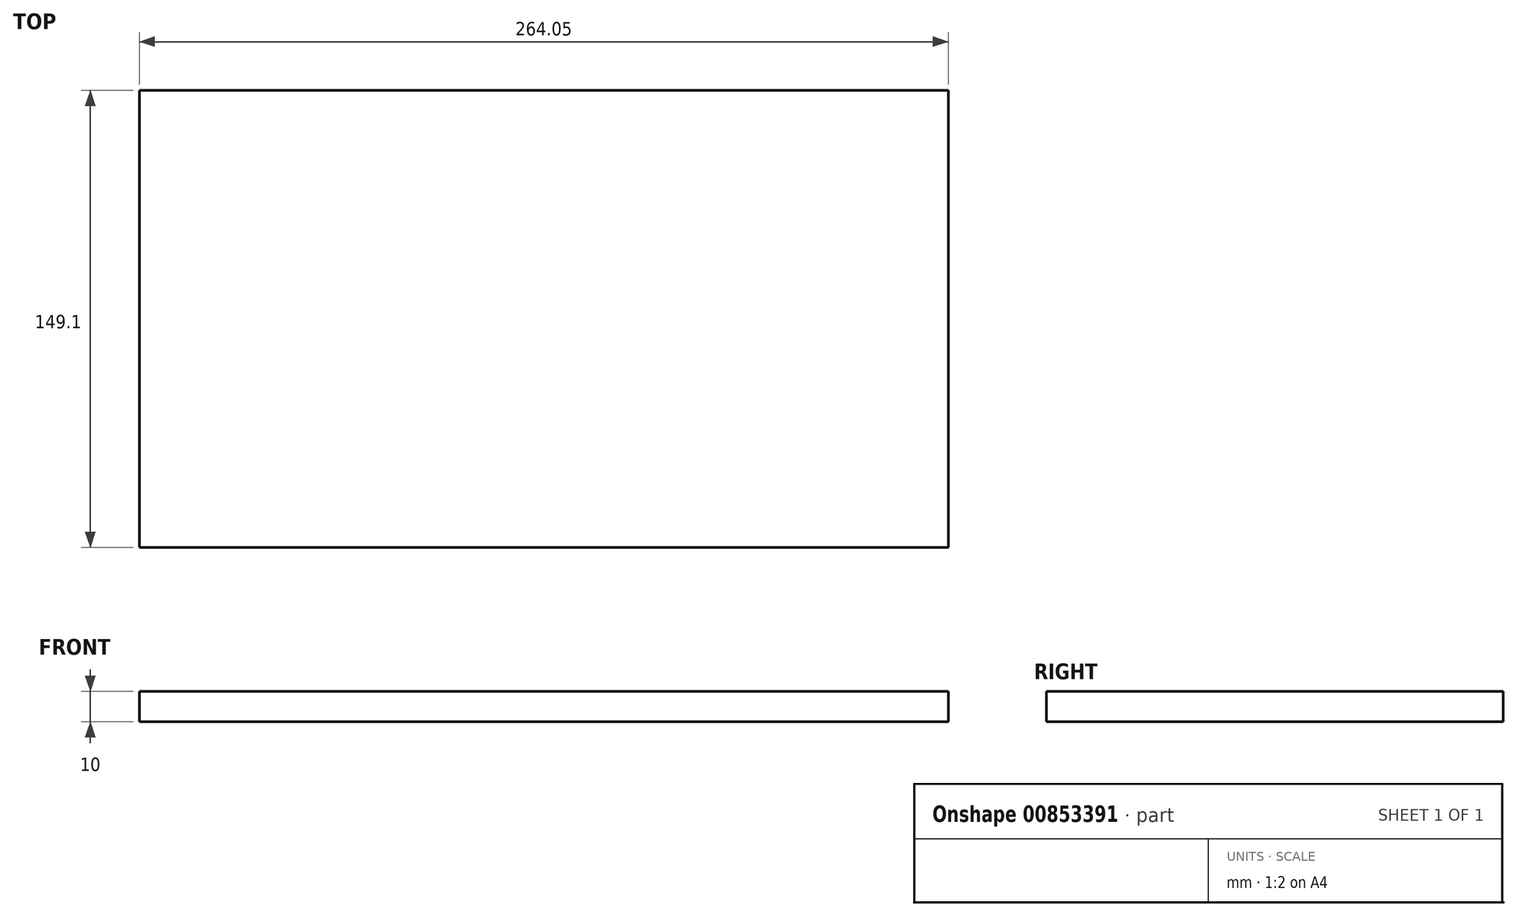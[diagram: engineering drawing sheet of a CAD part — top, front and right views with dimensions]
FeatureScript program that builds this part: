
annotation { "Feature Type Name" : "Feature", "Feature Type Description" : "" }
export const myFeature = defineFeature(function(context is Context, id is Id, definition is map)
    precondition{}
    {
        {
            var Q0;
            Q0=qCreatedBy(makeId("Top.planeOp"),FACE);
            var sketch = newSketch(context, id + "F0", { "sketchPlane" : qUnion([Q0])});
            skLineSegment(sketch, "E0.bottom", {"start": v(-132.25, 74.51) * mm, "end": v(131.8, 74.51) * mm});
            skLineSegment(sketch, "E0.top", {"start": v(-132.25, -74.59) * mm, "end": v(131.8, -74.59) * mm});
            skLineSegment(sketch, "E0.left", {"start": v(-132.25, 74.51) * mm, "end": v(-132.25, -74.59) * mm});
            skLineSegment(sketch, "E0.right", {"start": v(131.8, 74.51) * mm, "end": v(131.8, -74.59) * mm});
            skSolve(sketch);
        }
        {
            var Q0;
            Q0 = qSketchRegion(id + "F0", true);
            extrude(context, id + "F1", {"entities" : qUnion([Q0]), "depth" : 10 * mm, "offsetDistance" : 25.4 * mm});
        }
    });
